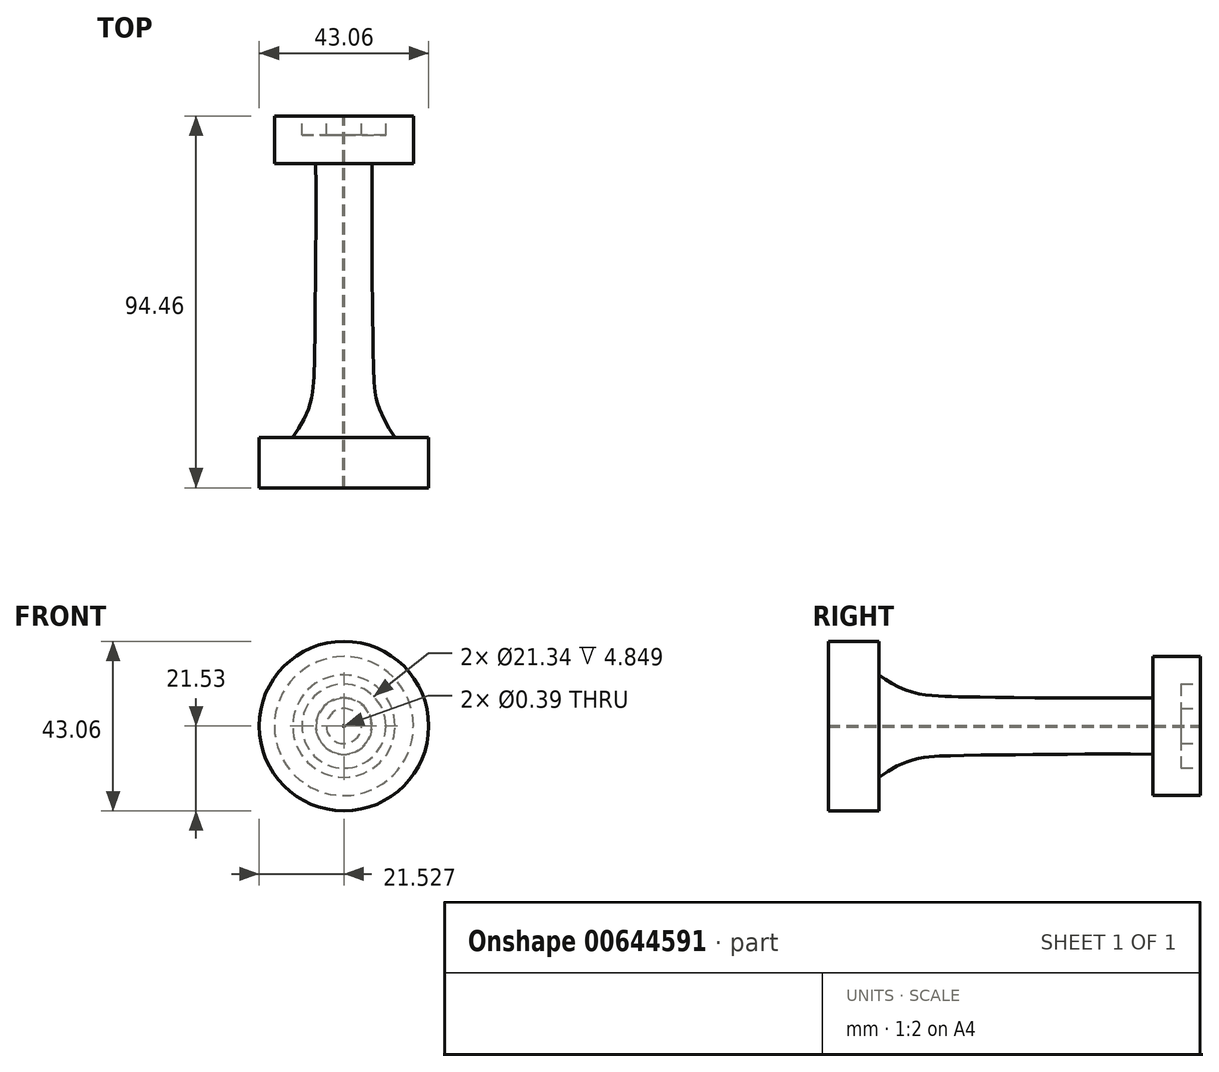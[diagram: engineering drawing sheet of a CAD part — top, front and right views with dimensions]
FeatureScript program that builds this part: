
annotation { "Feature Type Name" : "Feature", "Feature Type Description" : "" }
export const myFeature = defineFeature(function(context is Context, id is Id, definition is map)
    precondition{}
    {
        {
            var Q0;
            Q0=qCreatedBy(makeId("Top.planeOp"),FACE);
            var sketch = newSketch(context, id + "F0", { "sketchPlane" : qUnion([Q0])});
            skLineSegment(sketch, "E0", {"start": v(-33.65, 61.4) * mm, "end": v(-33.65, -50.33) * mm});
            skLineSegment(sketch, "E1", {"start": v(-33.65, -38.11) * mm, "end": v(-12.32, -38.11) * mm});
            skLineSegment(sketch, "E2", {"start": v(-12.32, -38.11) * mm, "end": v(-12.32, -25.9) * mm});
            skLineSegment(sketch, "E3", {"start": v(-12.32, -25.9) * mm, "end": v(-33.65, -25.9) * mm});
            skSolve(sketch);
        }
        {
            var Q0;
            Q0=qCreatedBy(makeId("Top.planeOp"),FACE);
            var sketch = newSketch(context, id + "F1", { "sketchPlane" : qUnion([Q0])});
            skFitSpline(sketch, "E4", {"points": [v(-20.66, -25.7) * mm, v(-24.15, -19.69) * mm, v(-25.7, -14.06) * mm, v(-26.09, -9.02) * mm, v(-26.28, 0) * mm, v(-26.48, 43.93) * mm, v(-26.09, 50.92) * mm], "startDerivative": vector(-28.98, 44.3) * mm, "endDerivative": vector(3.4, 35) * mm});
            skLineSegment(sketch, "E5", {"start": v(-26.48, 43.93) * mm, "end": v(-16, 43.93) * mm});
            skLineSegment(sketch, "E6", {"start": v(-16, 43.93) * mm, "end": v(-16, 55.96) * mm});
            skLineSegment(sketch, "E7", {"start": v(-16, 55.96) * mm, "end": v(-22.98, 55.96) * mm});
            skLineSegment(sketch, "E8", {"start": v(-22.98, 55.96) * mm, "end": v(-22.98, 51.1) * mm});
            skLineSegment(sketch, "E9", {"start": v(-22.98, 51.1) * mm, "end": v(-29.2, 51.1) * mm});
            skLineSegment(sketch, "E10", {"start": v(-29.2, 51.1) * mm, "end": v(-29.2, 55.96) * mm});
            skLineSegment(sketch, "E11", {"start": v(-29.2, 55.96) * mm, "end": v(-33.46, 55.96) * mm});
            skLineSegment(sketch, "E12", {"start": v(-33.46, 55.96) * mm, "end": v(-33.46, -38.5) * mm});
            skLineSegment(sketch, "E13", {"start": v(-33.46, -38.5) * mm, "end": v(-12.12, -38.5) * mm});
            skLineSegment(sketch, "E14", {"start": v(-12.12, -38.5) * mm, "end": v(-12.12, -25.7) * mm});
            skLineSegment(sketch, "E15", {"start": v(-12.12, -25.7) * mm, "end": v(-20.66, -25.7) * mm});
            skSolve(sketch);
        }
        {
            var Q0;
            Q0 = qSketchRegion(id + "F1", true);
            var Q1;
            Q1=sQuery(id+"F0.wireOp",EDGE,"E0");
            revolve(context, id + "F2", {"entities" : qUnion([Q0]), "axis" : qUnion([Q1]), "revolveType" : RevolveType.FULL});
        }
    });
